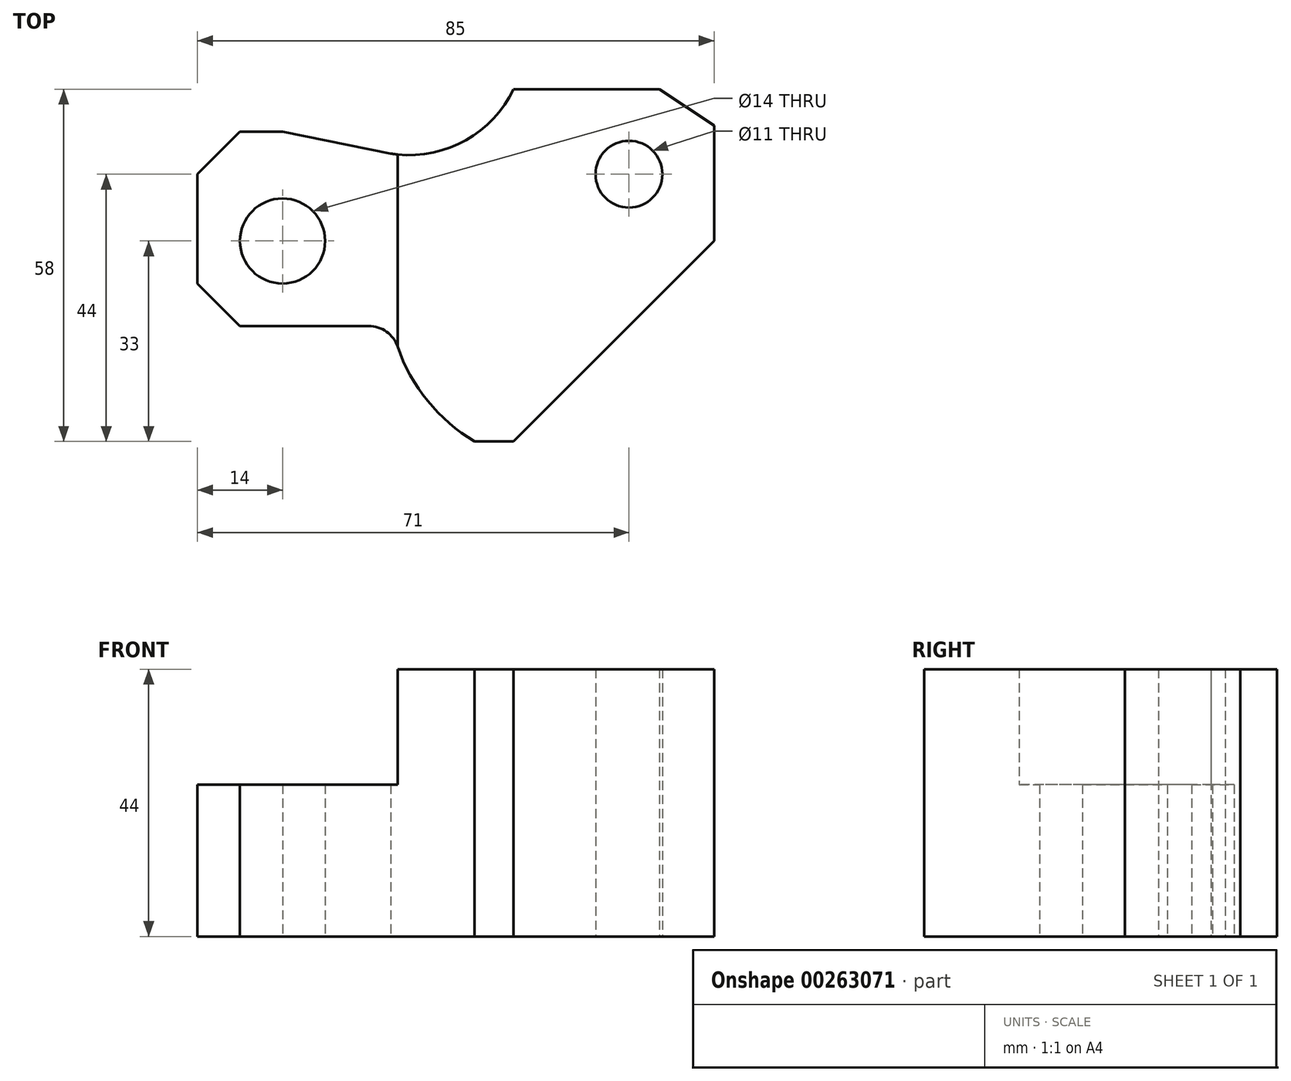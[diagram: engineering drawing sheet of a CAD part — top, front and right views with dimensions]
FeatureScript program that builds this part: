
annotation { "Feature Type Name" : "Feature", "Feature Type Description" : "" }
export const myFeature = defineFeature(function(context is Context, id is Id, definition is map)
    precondition{}
    {
        {
            var Q0;
            Q0=qCreatedBy(makeId("Top.planeOp"),FACE);
            var sketch = newSketch(context, id + "F0", { "sketchPlane" : qUnion([Q0])});
            skCircle(sketch, "E0", {"center": v(-21.37, 0.45) * mm, "radius": 7 * mm});
            skLineSegment(sketch, "E1", {"start": v(-21.37, 0.45) * mm, "end": v(-35.37, 0.45) * mm, "construction": true});
            skLineSegment(sketch, "E2", {"start": v(-35.37, 11.45) * mm, "end": v(-35.37, -6.55) * mm});
            skLineSegment(sketch, "E3", {"start": v(-35.37, -6.55) * mm, "end": v(-28.37, -13.55) * mm});
            skLineSegment(sketch, "E4", {"start": v(-35.37, 11.45) * mm, "end": v(-28.37, 18.45) * mm});
            skLineSegment(sketch, "E5", {"start": v(-28.37, -13.55) * mm, "end": v(-7.18, -13.55) * mm});
            skArc(sketch, "E6", {"start": v(-2.45, -16.94) * mm, "mid": v(-4.27, -14.48) * mm, "end": v(-7.18, -13.55) * mm});
            skLineSegment(sketch, "E7", {"start": v(-28.37, 18.45) * mm, "end": v(-21.37, 18.45) * mm});
            skLineSegment(sketch, "E8", {"start": v(49.63, 0.45) * mm, "end": v(49.63, 19.45) * mm});
            skLineSegment(sketch, "E9", {"start": v(49.63, 19.45) * mm, "end": v(40.63, 25.45) * mm});
            skLineSegment(sketch, "E10", {"start": v(16.63, -32.55) * mm, "end": v(10.25, -32.55) * mm});
            skArc(sketch, "E11", {"start": v(-2.45, -16.94) * mm, "mid": v(2.5, -25.88) * mm, "end": v(10.25, -32.55) * mm});
            skLineSegment(sketch, "E12", {"start": v(16.63, -32.55) * mm, "end": v(49.63, 0.45) * mm});
            skLineSegment(sketch, "E13", {"start": v(40.63, 25.45) * mm, "end": v(16.63, 25.45) * mm});
            skArc(sketch, "E14", {"start": v(-3.56, 14.84) * mm, "mid": v(8.3, 16.78) * mm, "end": v(16.63, 25.45) * mm});
            skLineSegment(sketch, "E15", {"start": v(-21.37, 18.45) * mm, "end": v(-3.56, 14.84) * mm});
            skCircle(sketch, "E16", {"center": v(35.63, 11.45) * mm, "radius": 5.5 * mm});
            skSolve(sketch);
        }
        {
            var Q0;
            Q0=makeQuery(id+"F0.imprint","IMPRINT",FACE,{"disambiguationData":[TD([[makeQuery(id+"F0.imprint","IMPRINT",EDGE,{"derivedFrom":sQuery(id+"F0.wireOp",EDGE,"E0")}),-1.0]])]});
            extrude(context, id + "F1", {"entities" : qUnion([Q0]), "depth" : 44 * mm});
        }
        {
            var Q0;
            Q0=makeQuery(id+"F1.opExtrude","CAP_FACE",FACE,{"disambiguationData":[OSD([sQuery(id+"F0.wireOp",EDGE,"E0"),sQuery(id+"F0.wireOp",EDGE,"E2"),sQuery(id+"F0.wireOp",EDGE,"E3"),sQuery(id+"F0.wireOp",EDGE,"E4"),sQuery(id+"F0.wireOp",EDGE,"E5"),sQuery(id+"F0.wireOp",EDGE,"E6"),sQuery(id+"F0.wireOp",EDGE,"E7"),sQuery(id+"F0.wireOp",EDGE,"E8"),sQuery(id+"F0.wireOp",EDGE,"E9"),sQuery(id+"F0.wireOp",EDGE,"E10"),sQuery(id+"F0.wireOp",EDGE,"E11"),sQuery(id+"F0.wireOp",EDGE,"E12"),sQuery(id+"F0.wireOp",EDGE,"E13"),sQuery(id+"F0.wireOp",EDGE,"E14"),sQuery(id+"F0.wireOp",EDGE,"E15"),sQuery(id+"F0.wireOp",EDGE,"E16")])],"isStart":false});
            var sketch = newSketch(context, id + "F2", { "sketchPlane" : qUnion([Q0])});
            skLineSegment(sketch, "E17", {"start": v(-2.45, 14.71) * mm, "end": v(-2.45, -16.94) * mm});
            skPoint(sketch, "E17.startSnap0", {"position": v(-31.87, 14.95) * mm});
            skLineSegment(sketch, "E18", {"start": v(-3.56, 14.84) * mm, "end": v(-21.37, 18.45) * mm});
            skLineSegment(sketch, "E19", {"start": v(-3.56, 14.84) * mm, "end": v(-2.45, 14.71) * mm});
            skLineSegment(sketch, "E20", {"start": v(-21.37, 18.45) * mm, "end": v(-28.37, 18.45) * mm});
            skLineSegment(sketch, "E21", {"start": v(-28.37, 18.45) * mm, "end": v(-35.37, 11.45) * mm});
            skLineSegment(sketch, "E22", {"start": v(-35.37, 11.45) * mm, "end": v(-35.37, -6.55) * mm});
            skLineSegment(sketch, "E23", {"start": v(-35.37, -6.55) * mm, "end": v(-28.37, -13.55) * mm});
            skLineSegment(sketch, "E24", {"start": v(-28.37, -13.55) * mm, "end": v(-7.18, -13.55) * mm});
            skArc(sketch, "E25", {"start": v(-2.45, -16.94) * mm, "mid": v(-4.27, -14.48) * mm, "end": v(-7.18, -13.55) * mm});
            skSolve(sketch);
        }
        {
            var Q0;
            {var subQ0=sQuery(id+"F2.wireOp",EDGE,"E18");Q0=makeQuery(id+"F2.imprint","IMPRINT",FACE,{"disambiguationData":[TD([[makeQuery(id+"F2.imprint","IMPRINT",EDGE,{"derivedFrom":subQ0}),-1.0]])]});}
            extrude(context, id + "F3", {"entities" : qUnion([Q0]), "operationType" : NewBodyOperationType.REMOVE, "oppositeDirection" : true, "depth" : 19 * mm});
        }
        {
            var Q0;
            Q0=makeQuery(id+"F1.opExtrude","CAP_FACE",FACE,{"disambiguationData":[OSD([sQuery(id+"F0.wireOp",EDGE,"E0"),sQuery(id+"F0.wireOp",EDGE,"E2"),sQuery(id+"F0.wireOp",EDGE,"E3"),sQuery(id+"F0.wireOp",EDGE,"E4"),sQuery(id+"F0.wireOp",EDGE,"E5"),sQuery(id+"F0.wireOp",EDGE,"E6"),sQuery(id+"F0.wireOp",EDGE,"E7"),sQuery(id+"F0.wireOp",EDGE,"E8"),sQuery(id+"F0.wireOp",EDGE,"E9"),sQuery(id+"F0.wireOp",EDGE,"E10"),sQuery(id+"F0.wireOp",EDGE,"E11"),sQuery(id+"F0.wireOp",EDGE,"E12"),sQuery(id+"F0.wireOp",EDGE,"E13"),sQuery(id+"F0.wireOp",EDGE,"E14"),sQuery(id+"F0.wireOp",EDGE,"E15"),sQuery(id+"F0.wireOp",EDGE,"E16")])],"isStart":false});
            cPlane(context, id + "F4", {"entities" : qUnion([Q0]), "cplaneType" : CPlaneType.OFFSET, "offset" : 24 * mm, "oppositeDirection" : true, "width" : 150 * mm, "height" : 150 * mm});
        }
    });
